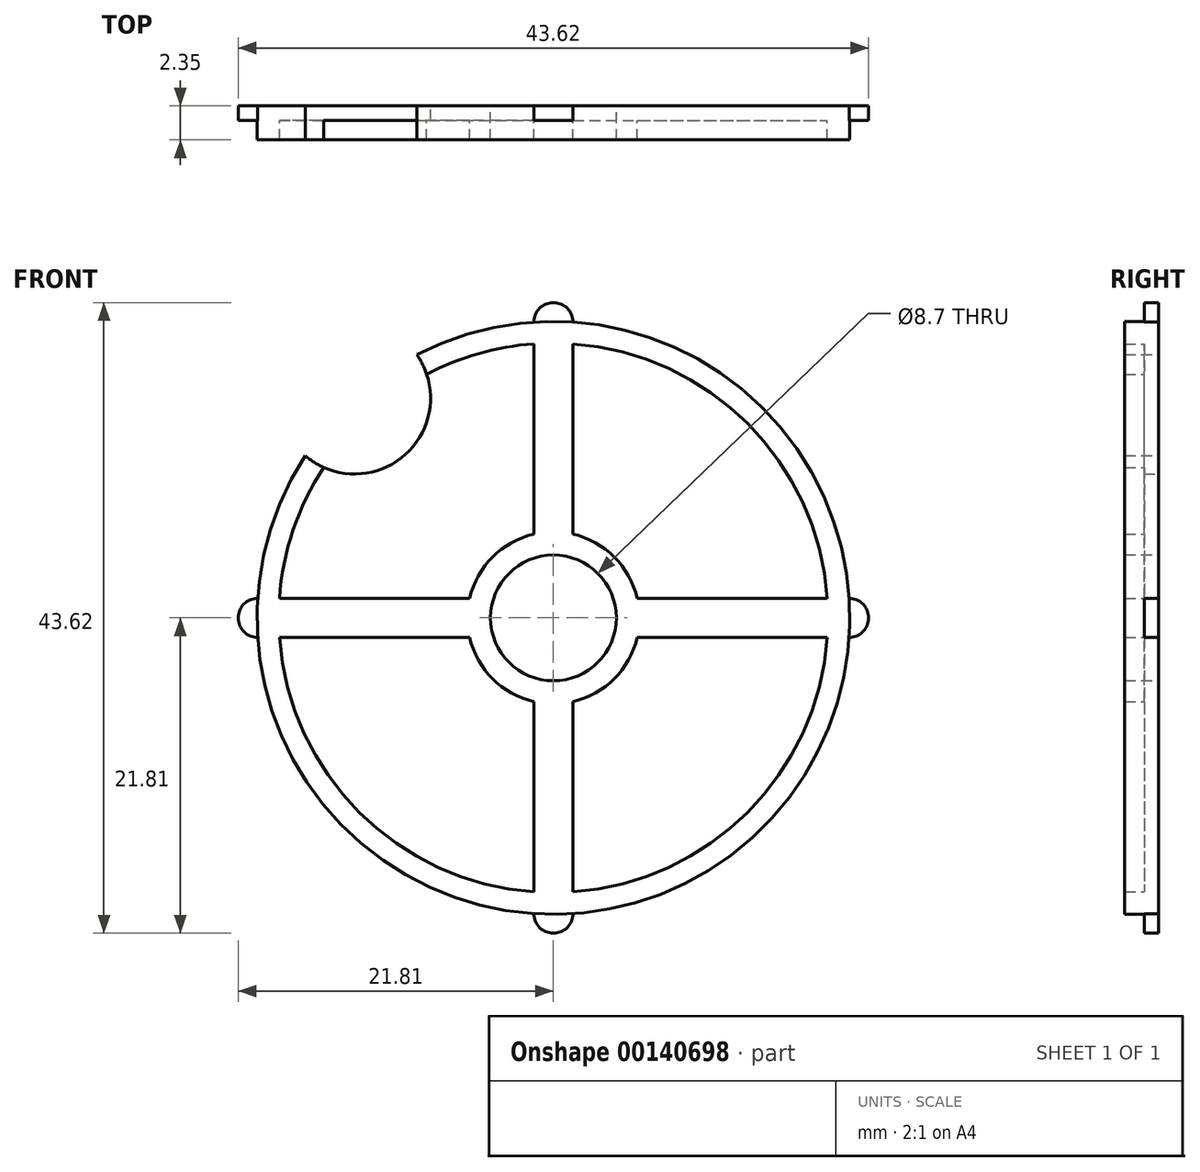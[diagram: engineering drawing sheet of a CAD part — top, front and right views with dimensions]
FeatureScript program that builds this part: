
annotation { "Feature Type Name" : "Feature", "Feature Type Description" : "" }
export const myFeature = defineFeature(function(context is Context, id is Id, definition is map)
    precondition{}
    {
        {
            var Q0;
            Q0=qCreatedBy(makeId("Front.planeOp"),FACE);
            var sketch = newSketch(context, id + "F0", { "sketchPlane" : qUnion([Q0])});
            skCircle(sketch, "E0", {"center": v(0, 0) * mm, "radius": 19 * mm});
            skCircle(sketch, "E1", {"center": v(0, 0) * mm, "radius": 5.95 * mm});
            skLineSegment(sketch, "E2", {"start": v(-1.35, 5.8) * mm, "end": v(-1.35, 18.95) * mm});
            skLineSegment(sketch, "E3", {"start": v(1.35, 5.8) * mm, "end": v(1.35, 18.95) * mm});
            skLineSegment(sketch, "E4", {"start": v(-1.35, -5.8) * mm, "end": v(-1.35, -18.95) * mm});
            skLineSegment(sketch, "E5", {"start": v(1.35, -5.8) * mm, "end": v(1.35, -18.95) * mm});
            skLineSegment(sketch, "E6", {"start": v(-5.8, 1.35) * mm, "end": v(-18.95, 1.35) * mm});
            skLineSegment(sketch, "E7", {"start": v(-5.8, -1.35) * mm, "end": v(-18.95, -1.35) * mm});
            skLineSegment(sketch, "E8", {"start": v(5.8, 1.35) * mm, "end": v(18.95, 1.35) * mm});
            skLineSegment(sketch, "E9", {"start": v(5.8, -1.35) * mm, "end": v(18.95, -1.35) * mm});
            skCircle(sketch, "E10", {"center": v(0, 0) * mm, "radius": 20.5 * mm});
            skCircle(sketch, "E11", {"center": v(0, 0) * mm, "radius": 4.35 * mm});
            skArc(sketch, "E12", {"start": v(-17.16, 11.2) * mm, "mid": v(-10.23, 11.3) * mm, "end": v(-9.44, 18.2) * mm});
            skLineSegment(sketch, "E13", {"start": v(-1.35, 18.95) * mm, "end": v(-1.35, 20.46) * mm, "construction": true});
            skLineSegment(sketch, "E14", {"start": v(1.35, 18.95) * mm, "end": v(1.35, 20.46) * mm, "construction": true});
            skArc(sketch, "E15", {"start": v(1.35, 20.46) * mm, "mid": v(0, 21.8) * mm, "end": v(-1.35, 20.46) * mm});
            skLineSegment(sketch, "E16", {"start": v(-18.95, 1.35) * mm, "end": v(-20.46, 1.35) * mm, "construction": true});
            skLineSegment(sketch, "E17", {"start": v(-18.95, -1.35) * mm, "end": v(-20.46, -1.35) * mm, "construction": true});
            skArc(sketch, "E18", {"start": v(-20.46, 1.35) * mm, "mid": v(-21.8, 0) * mm, "end": v(-20.46, -1.35) * mm});
            skLineSegment(sketch, "E19", {"start": v(-1.35, -18.95) * mm, "end": v(-1.35, -20.46) * mm, "construction": true});
            skLineSegment(sketch, "E20", {"start": v(1.35, -18.95) * mm, "end": v(1.35, -20.46) * mm, "construction": true});
            skArc(sketch, "E21", {"start": v(-1.35, -20.46) * mm, "mid": v(0, -21.8) * mm, "end": v(1.35, -20.46) * mm});
            skLineSegment(sketch, "E22", {"start": v(18.95, 1.35) * mm, "end": v(20.46, 1.35) * mm, "construction": true});
            skLineSegment(sketch, "E23", {"start": v(18.95, -1.35) * mm, "end": v(20.46, -1.35) * mm, "construction": true});
            skArc(sketch, "E24", {"start": v(20.46, -1.35) * mm, "mid": v(21.8, 0) * mm, "end": v(20.46, 1.35) * mm});
            skSolve(sketch);
        }
        {
            var Q0;
            {var subQ11=sQuery(id+"F0.wireOp",EDGE,"E0");var subQ14=makeQuery(id+"F0.imprint","INTERSECT",VERTEX,{"derivedFrom":[subQ11,sQuery(id+"F0.wireOp",EDGE,"E3")]});Q0=makeQuery(id+"F0.imprint","IMPRINT",FACE,{"disambiguationData":[TD([[makeQuery(id+"F0.imprint","IMPRINT",EDGE,{"disambiguationData":[TD([[subQ14,1.0]])],"derivedFrom":subQ11}),-1.0]])]});}
            var Q1;
            Q1=makeQuery(id+"F0.imprint","IMPRINT",FACE,{"disambiguationData":[TD([[makeQuery(id+"F0.imprint","IMPRINT",EDGE,{"derivedFrom":sQuery(id+"F0.wireOp",EDGE,"E11")}),-1.0]])]});
            var Q2;
            {var subQ0=sQuery(id+"F0.wireOp",EDGE,"E6");Q2=makeQuery(id+"F0.imprint","IMPRINT",FACE,{"disambiguationData":[TD([[makeQuery(id+"F0.imprint","IMPRINT",EDGE,{"derivedFrom":subQ0}),1.0]])]});}
            var Q3;
            {var subQ0=sQuery(id+"F0.wireOp",EDGE,"E2");Q3=makeQuery(id+"F0.imprint","IMPRINT",FACE,{"disambiguationData":[TD([[makeQuery(id+"F0.imprint","IMPRINT",EDGE,{"derivedFrom":subQ0}),-1.0]])]});}
            var Q4;
            {var subQ0=sQuery(id+"F0.wireOp",EDGE,"E8");Q4=makeQuery(id+"F0.imprint","IMPRINT",FACE,{"disambiguationData":[TD([[makeQuery(id+"F0.imprint","IMPRINT",EDGE,{"derivedFrom":subQ0}),-1.0]])]});}
            var Q5;
            {var subQ0=sQuery(id+"F0.wireOp",EDGE,"E4");Q5=makeQuery(id+"F0.imprint","IMPRINT",FACE,{"disambiguationData":[TD([[makeQuery(id+"F0.imprint","IMPRINT",EDGE,{"derivedFrom":subQ0}),1.0]])]});}
            extrude(context, id + "F1", {"entities" : qUnion([Q0, Q1, Q2, Q3, Q4, Q5]), "depth" : 2.35 * mm});
        }
        {
            var Q0;
            {var subQ0=sQuery(id+"F0.wireOp",EDGE,"E2");Q0=makeQuery(id+"F0.imprint","IMPRINT",FACE,{"disambiguationData":[TD([[makeQuery(id+"F0.imprint","IMPRINT",EDGE,{"derivedFrom":subQ0}),1.0]])]});}
            var Q1;
            {var subQ0=sQuery(id+"F0.wireOp",EDGE,"E3");Q1=makeQuery(id+"F0.imprint","IMPRINT",FACE,{"disambiguationData":[TD([[makeQuery(id+"F0.imprint","IMPRINT",EDGE,{"derivedFrom":subQ0}),-1.0]])]});}
            var Q2;
            {var subQ0=sQuery(id+"F0.wireOp",EDGE,"E5");Q2=makeQuery(id+"F0.imprint","IMPRINT",FACE,{"disambiguationData":[TD([[makeQuery(id+"F0.imprint","IMPRINT",EDGE,{"derivedFrom":subQ0}),1.0]])]});}
            var Q3;
            {var subQ0=sQuery(id+"F0.wireOp",EDGE,"E4");Q3=makeQuery(id+"F0.imprint","IMPRINT",FACE,{"disambiguationData":[TD([[makeQuery(id+"F0.imprint","IMPRINT",EDGE,{"derivedFrom":subQ0}),-1.0]])]});}
            var Q4;
            {var subQ0=sQuery(id+"F0.wireOp",EDGE,"E18");Q4=makeQuery(id+"F0.imprint","IMPRINT",FACE,{"disambiguationData":[TD([[makeQuery(id+"F0.imprint","IMPRINT",EDGE,{"derivedFrom":subQ0}),1.0]])]});}
            var Q5;
            {var subQ0=sQuery(id+"F0.wireOp",EDGE,"E15");Q5=makeQuery(id+"F0.imprint","IMPRINT",FACE,{"disambiguationData":[TD([[makeQuery(id+"F0.imprint","IMPRINT",EDGE,{"derivedFrom":subQ0}),1.0]])]});}
            var Q6;
            {var subQ0=sQuery(id+"F0.wireOp",EDGE,"E24");Q6=makeQuery(id+"F0.imprint","IMPRINT",FACE,{"disambiguationData":[TD([[makeQuery(id+"F0.imprint","IMPRINT",EDGE,{"derivedFrom":subQ0}),1.0]])]});}
            var Q7;
            {var subQ0=sQuery(id+"F0.wireOp",EDGE,"E21");Q7=makeQuery(id+"F0.imprint","IMPRINT",FACE,{"disambiguationData":[TD([[makeQuery(id+"F0.imprint","IMPRINT",EDGE,{"derivedFrom":subQ0}),1.0]])]});}
            extrude(context, id + "F2", {"entities" : qUnion([Q0, Q1, Q2, Q3, Q4, Q5, Q6, Q7]), "operationType" : NewBodyOperationType.ADD, "depth" : 1 * mm});
        }
    });
